# Revit family: baryer iskrozashchity BISSh
name_source: partatom
category: Датчики
units: mm (PartAtom-declared; Revit-internal decimal feet)

## family parameters
Всегда вертикально = Да
Заголовок OmniClass = Communication and Data Processing Equipment
На основе рабочей плоскости = Нет
Номер OmniClass = 23.85.50.17
Общий = Нет
При загрузке вырезать с полостями = Нет
Размер круглого соединителя = Использовать диаметр
Сохранять ориентацию аннотаций = Нет
Тип детали = Нормальный
Точка принадлежности помещению = Нет

## types (1)
- Барьер искрозащиты шлейфа «БИСШ»
    ADSK_Единица измерения = шт.
    ADSK_Завод-изготовитель = ООО НПП «МАГНИТО-КОНТАКТ»
    ADSK_Масса = 0.6
    ADSK_Материал = Пластик белый
    ADSK_Наименование = Пассивный барьер искрозащиты БИСШ
    ADSK_Наименование краткое = БИСШ
    ADSK_Обозначение = АТФЕ.426439.001 ТУ
    ADSK_Примечание = Для обеспечения взрывозащиты электрических цепей устройств, размещаемых во взрывоопасной зоне, производитель рекомендует применить активный барьер искрозащиты АБИ ПАШК.426439.146 ТУ (Маркировка взрывозащиты [Ex ia Ga] IIB/IIC).
    ADSK_Размер_Высота = 67 мм
    ADSK_Размер_Длина = 120 мм
    ADSK_Размер_Ширина = 152 мм
    URL = https://m-kontakt.ru
    Изготовитель = ООО НПП «МАГНИТО-КОНТАКТ»
    Метизы = Металл
    Напряжение на входных клеммах = не более, В 28.4
    Описание = Барьер искрозащиты шлейфа «БИСШ» предназначен для обеспечения искробезопасности одного шлейфа пожарной или охранной сигнализации, с включенными в него пожарными или охранными извещателями, датчиками с нормально замкнутыми или разомкнутыми контактами, а также извещателями, питаемыми по шлейфу сигнализации с уровнем искрозащиты «ia» для взрывозащищенного электрооборудования группы II, подгрупп IIC/IIB по ГОСТ 30852.10-2002 (МЭК 60079-11:1999). БИСШ предназначен для размещения вне взрывоопасной зоны.Барьер искрозащиты шлейфа «БИСШ» является пассивным барьером, относится к классу связанного электрооборудования предназначенного для установке вне взрывоопасных зон и имеет маркировку по взрывозащите [Exia]IIC/IIB по ГОСТ 30852.0-2002 (МЭК 60079-0:1998). «БИСШ» соответствует требованиям технического регламента Таможенного союза ТР ТС 012/2011 «О безопасности оборудования для работы во взрывоопасных средах», устанавливающего на единой таможенной территории Таможенного союза единые обязательные для применения и исполнения требования к оборудования для работы во взрывоопасных средах.
    Отметка по умолчанию = 0 мм
    Сопротивление, вносимое БИСШ в шлейф = в пределах, Ом от 620 до 700
    Степень защиты оболочки = IP 54
    Температура работы = от минус 20° до плюс 40°С
